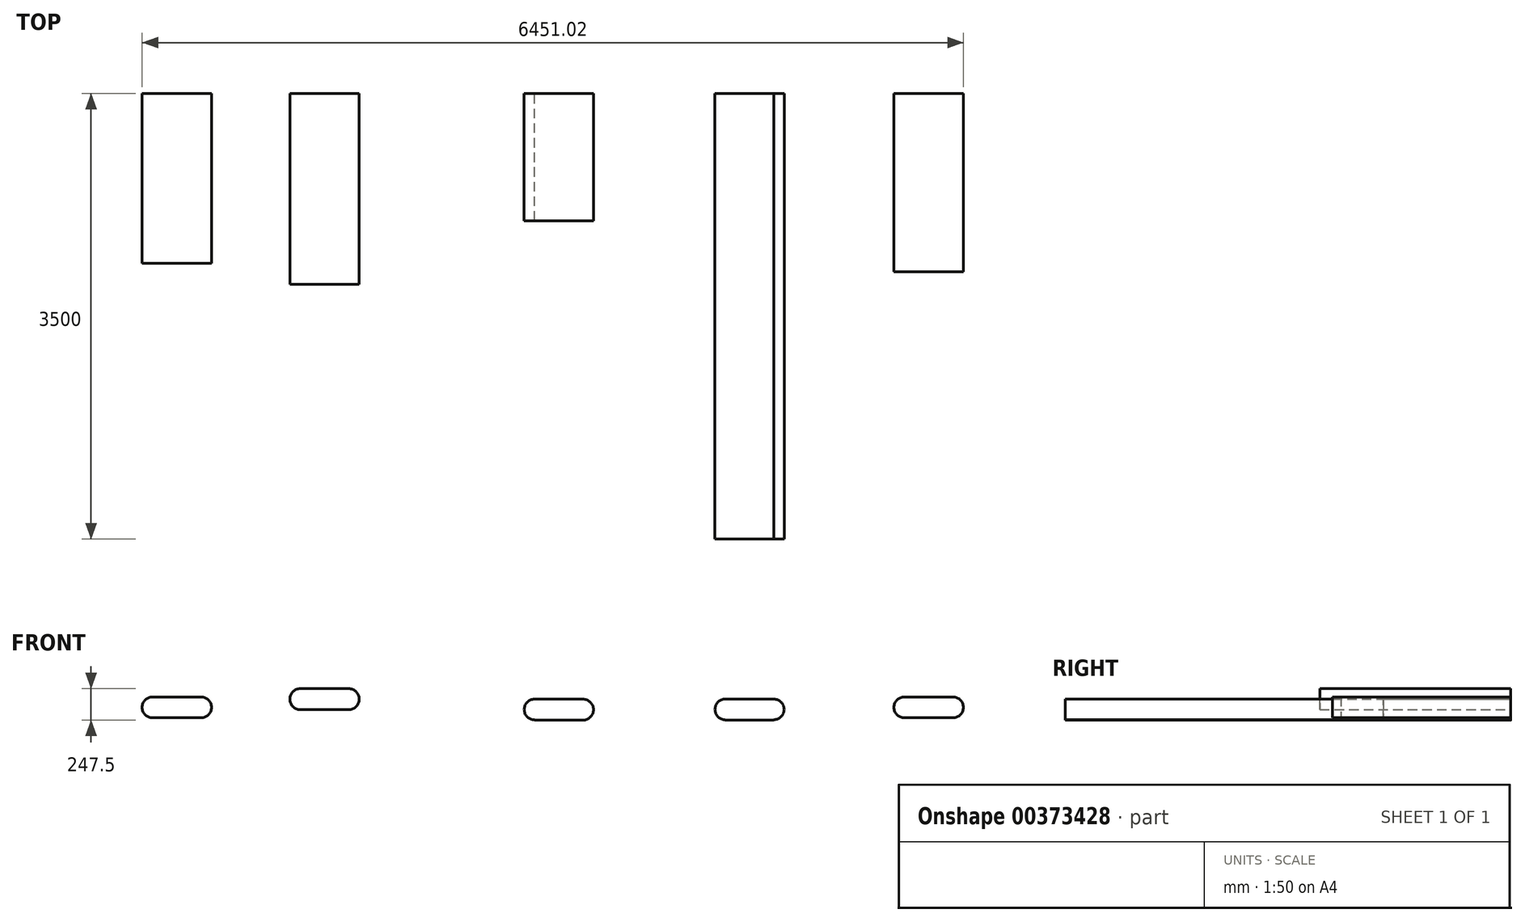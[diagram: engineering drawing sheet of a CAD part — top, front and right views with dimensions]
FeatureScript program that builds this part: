
annotation { "Feature Type Name" : "Feature", "Feature Type Description" : "" }
export const myFeature = defineFeature(function(context is Context, id is Id, definition is map)
    precondition{}
    {
        {
            var Q0;
            Q0=qCreatedBy(makeId("Front.planeOp"),FACE);
            var sketch = newSketch(context, id + "F0", { "sketchPlane" : qUnion([Q0])});
            skLineSegment(sketch, "E0.bottom", {"start": v(190, -82.5) * mm, "end": v(-190, -82.5) * mm});
            skLineSegment(sketch, "E0.top", {"start": v(190, 82.5) * mm, "end": v(-190, 82.5) * mm});
            skPoint(sketch, "E0.middle", {"position": v(0, 0) * mm});
            skArc(sketch, "E1", {"start": v(-190, 82.5) * mm, "mid": v(-272.5, 0) * mm, "end": v(-190, -82.5) * mm});
            skArc(sketch, "E2", {"start": v(190, -82.5) * mm, "mid": v(272.5, 0) * mm, "end": v(190, 82.5) * mm});
            skSolve(sketch);
        }
        {
            var Q0;
            Q0=makeQuery(id+"F0.imprint","IMPRINT",FACE,{"disambiguationData":[TD([[makeQuery(id+"F0.imprint","IMPRINT",EDGE,{"derivedFrom":sQuery(id+"F0.wireOp",EDGE,"E0.bottom")}),-1.0]])]});
            extrude(context, id + "F1", {"entities" : qUnion([Q0]), "depth" : 1335 * mm});
        }
        {
            var Q0;
            Q0=qCreatedBy(makeId("Front.planeOp"),FACE);
            var sketch = newSketch(context, id + "F2", { "sketchPlane" : qUnion([Q0])});
            skLineSegment(sketch, "E3.bottom", {"start": v(1349.94, -17.83) * mm, "end": v(969.94, -17.83) * mm});
            skLineSegment(sketch, "E3.top", {"start": v(1349.94, 147.17) * mm, "end": v(969.94, 147.17) * mm});
            skPoint(sketch, "E3.middle", {"position": v(1159.94, 64.67) * mm});
            skArc(sketch, "E4", {"start": v(969.94, 147.17) * mm, "mid": v(887.44, 64.67) * mm, "end": v(969.94, -17.83) * mm});
            skArc(sketch, "E5", {"start": v(1349.94, -17.83) * mm, "mid": v(1432.44, 64.67) * mm, "end": v(1349.94, 147.17) * mm});
            skSolve(sketch);
        }
        {
            var Q0;
            Q0=makeQuery(id+"F2.imprint","IMPRINT",FACE,{"disambiguationData":[TD([[makeQuery(id+"F2.imprint","IMPRINT",EDGE,{"derivedFrom":sQuery(id+"F2.wireOp",EDGE,"E3.bottom")}),-1.0]])]});
            extrude(context, id + "F3", {"entities" : qUnion([Q0]), "depth" : 1500 * mm});
        }
        {
            var Q0;
            Q0=makeQuery(id+"F3.opExtrude","CAP_FACE",FACE,{"disambiguationData":[OSD([sQuery(id+"F2.wireOp",EDGE,"E3.bottom"),sQuery(id+"F2.wireOp",EDGE,"E3.top"),sQuery(id+"F2.wireOp",EDGE,"E4"),sQuery(id+"F2.wireOp",EDGE,"E5")])],"isStart":true});
            var sketch = newSketch(context, id + "F4", { "sketchPlane" : qUnion([Q0])});
            skLineSegment(sketch, "E6", {"start": v(0, 0) * mm, "end": v(-2999.95, -17.83) * mm, "construction": true});
            skPoint(sketch, "E6.endSnap0", {"position": v(-1159.94, -17.83) * mm});
            skLineSegment(sketch, "E7.bottom", {"start": v(-3189.95, -100.33) * mm, "end": v(-2809.95, -100.33) * mm});
            skLineSegment(sketch, "E7.top", {"start": v(-3189.95, 64.67) * mm, "end": v(-2809.95, 64.67) * mm});
            skLineSegment(sketch, "E7.right", {"start": v(-2809.95, -100.33) * mm, "end": v(-2809.95, -98.07) * mm});
            skPoint(sketch, "E7.middle", {"position": v(-2999.95, -17.83) * mm});
            skArc(sketch, "E8", {"start": v(-2809.95, -98.07) * mm, "mid": v(-2728.58, -16.7) * mm, "end": v(-2809.95, 64.67) * mm});
            skPoint(sketch, "E8.centerSnap0", {"position": v(-2809.95, -17.83) * mm});
            skArc(sketch, "E9", {"start": v(-3189.95, 64.67) * mm, "mid": v(-3272.45, -17.83) * mm, "end": v(-3189.95, -100.33) * mm});
            skLineSegment(sketch, "E10.trimOffspring", {"start": v(-2809.95, -17.83) * mm, "end": v(-2809.95, -16.7) * mm});
            skSolve(sketch);
        }
        {
            var Q0;
            Q0=makeQuery(id+"F4.imprint","IMPRINT",FACE,{"disambiguationData":[TD([[makeQuery(id+"F4.imprint","IMPRINT",EDGE,{"derivedFrom":sQuery(id+"F4.wireOp",EDGE,"E7.bottom")}),1.0]])]});
            extrude(context, id + "F5", {"entities" : qUnion([Q0]), "oppositeDirection" : true, "depth" : 1000 * mm});
        }
        {
            var Q0;
            Q0=makeQuery(id+"F5.opExtrude","CAP_FACE",FACE,{"disambiguationData":[OSD([sQuery(id+"F4.wireOp",EDGE,"E7.bottom"),sQuery(id+"F4.wireOp",EDGE,"E7.top"),sQuery(id+"F4.wireOp",EDGE,"E7.right"),sQuery(id+"F4.wireOp",EDGE,"E8"),sQuery(id+"F4.wireOp",EDGE,"E9")])],"isStart":true});
            var sketch = newSketch(context, id + "F6", { "sketchPlane" : qUnion([Q0])});
            skPoint(sketch, "E11.startSnap0", {"position": v(-2999.95, -100.33) * mm});
            skLineSegment(sketch, "E12", {"start": v(-2999.95, -15.92) * mm, "end": v(-4499.95, -15.92) * mm, "construction": true});
            skLineSegment(sketch, "E13.bottom", {"start": v(-4689.95, -98.42) * mm, "end": v(-4309.95, -98.42) * mm});
            skLineSegment(sketch, "E13.top", {"start": v(-4689.95, 66.58) * mm, "end": v(-4309.95, 66.58) * mm});
            skLineSegment(sketch, "E13.left", {"start": v(-4689.95, -98.42) * mm, "end": v(-4689.95, -96.5) * mm});
            skPoint(sketch, "E13.middle", {"position": v(-4499.95, -15.92) * mm});
            skArc(sketch, "E14", {"start": v(-4309.95, -98.42) * mm, "mid": v(-4227.45, -15.92) * mm, "end": v(-4309.95, 66.58) * mm});
            skArc(sketch, "E15", {"start": v(-4689.95, 64.67) * mm, "mid": v(-4770.53, -15.92) * mm, "end": v(-4689.95, -96.5) * mm});
            skLineSegment(sketch, "E16.trimOffspring", {"start": v(-4689.95, 64.67) * mm, "end": v(-4689.95, 66.58) * mm});
            skSolve(sketch);
        }
        {
            var Q0;
            Q0=makeQuery(id+"F6.imprint","IMPRINT",FACE,{"disambiguationData":[TD([[makeQuery(id+"F6.imprint","IMPRINT",EDGE,{"derivedFrom":sQuery(id+"F6.wireOp",EDGE,"E13.bottom")}),1.0]])]});
            extrude(context, id + "F7", {"entities" : qUnion([Q0]), "oppositeDirection" : true, "depth" : 3500 * mm});
        }
        {
            var Q0;
            Q0=makeQuery(id+"F6.imprint","IMPRINT",FACE,{"disambiguationData":[TD([[makeQuery(id+"F6.imprint","IMPRINT",EDGE,{"derivedFrom":sQuery(id+"F6.wireOp",EDGE,"E13.bottom")}),1.0]])]});
            var sketch = newSketch(context, id + "F8", { "sketchPlane" : qUnion([Q0])});
            skLineSegment(sketch, "E17", {"start": v(-4406.02, 0) * mm, "end": v(-5906.02, 0) * mm, "construction": true});
            skLineSegment(sketch, "E18.bottom", {"start": v(-6096.02, -82.5) * mm, "end": v(-5716.02, -82.5) * mm});
            skLineSegment(sketch, "E18.top", {"start": v(-6096.02, 82.5) * mm, "end": v(-5716.02, 82.5) * mm});
            skPoint(sketch, "E18.middle", {"position": v(-5906.02, 0) * mm});
            skArc(sketch, "E19", {"start": v(-5716.02, -82.5) * mm, "mid": v(-5633.52, 0) * mm, "end": v(-5716.02, 82.5) * mm});
            skArc(sketch, "E20", {"start": v(-6096.02, 82.5) * mm, "mid": v(-6178.52, 0) * mm, "end": v(-6096.02, -82.5) * mm});
            skSolve(sketch);
        }
        {
            var Q0;
            Q0=makeQuery(id+"F8.imprint","IMPRINT",FACE,{"disambiguationData":[TD([[makeQuery(id+"F8.imprint","IMPRINT",EDGE,{"derivedFrom":sQuery(id+"F8.wireOp",EDGE,"E18.bottom")}),1.0]])]});
            extrude(context, id + "F9", {"entities" : qUnion([Q0]), "oppositeDirection" : true, "depth" : 1400 * mm});
        }
    });
